# Revit family: Fleetwood Picnic Table and Bench
name_source: partatom
category: Furniture Systems
revit_build: Autodesk Revit 2018 (Build: 20170223_1515(x64)
units: mm (PartAtom-declared; Revit-internal decimal feet)

## family parameters
Always vertical = Yes
Cut with Voids When Loaded = No
Part Type = Normal
Room Calculation Point = No
Round Connector Dimension = Use Diameter
Shared = No
Work Plane-Based = No

## types (7) — shared parameters
Assembly Code = E2020200
Description = Fleetwood Picnic Table and Bench
Manufacturer = Fleetwood Furniture
Model = PT.RS
Painted Frame Material = Fleetwood Painted Frame Paint Silver 4799 Hybrid
Top Edge Material = Fleetwood Surface White Pionite/Panolam S411
Top Surface Material = Fleetwood Edgeband White Pionite/Panolam S411
Top Thickness = 0' - 1"
URL = https://www.fleetwoodfurniture.com

## per-type parameters (varying)
| type | Actual Depth | Actual Height | Actual Width | Bench | Depth | Height | Table | Width |
| Table 60w x 30d x 24h | 2' - 6" | 2' - 0" | 5' - 0" | No | 2' - 6" | 2' - 0" | Yes | 5' - 0" |
| Table 60w x 30d x 29h | 2' - 6" | 2' - 5" | 5' - 0" | No | 2' - 6" | 2' - 5" | Yes | 5' - 0" |
| Table 60w x 36d x 29h | 3' - 0" | 2' - 5" | 5' - 0" | No | 3' - 0" | 2' - 5" | Yes | 5' - 0" |
| Table 72w x 36d x 29h | 3' - 0" | 2' - 5" | 6' - 0" | No | 3' - 0" | 2' - 5" | Yes | 6' - 0" |
| Bench 51w x 15d x 14h | 1' - 3" | 1' - 2" | 4' - 3" | Yes | 1' - 3" | 1' - 2" | No | 4' - 3" |
| Bench 51w x 15d x 18h | 1' - 3" | 1' - 6" | 4' - 3" | Yes | 1' - 3" | 1' - 6" | No | 4' - 3" |
| Bench 63w x 15d x 18h | 1' - 3" | 1' - 6" | 5' - 3" | Yes | 1' - 3" | 1' - 6" | No | 5' - 3" |

## geometry (parser evidence)
native form markers: Sweep x6
no freeform markers — native parametric forms only
